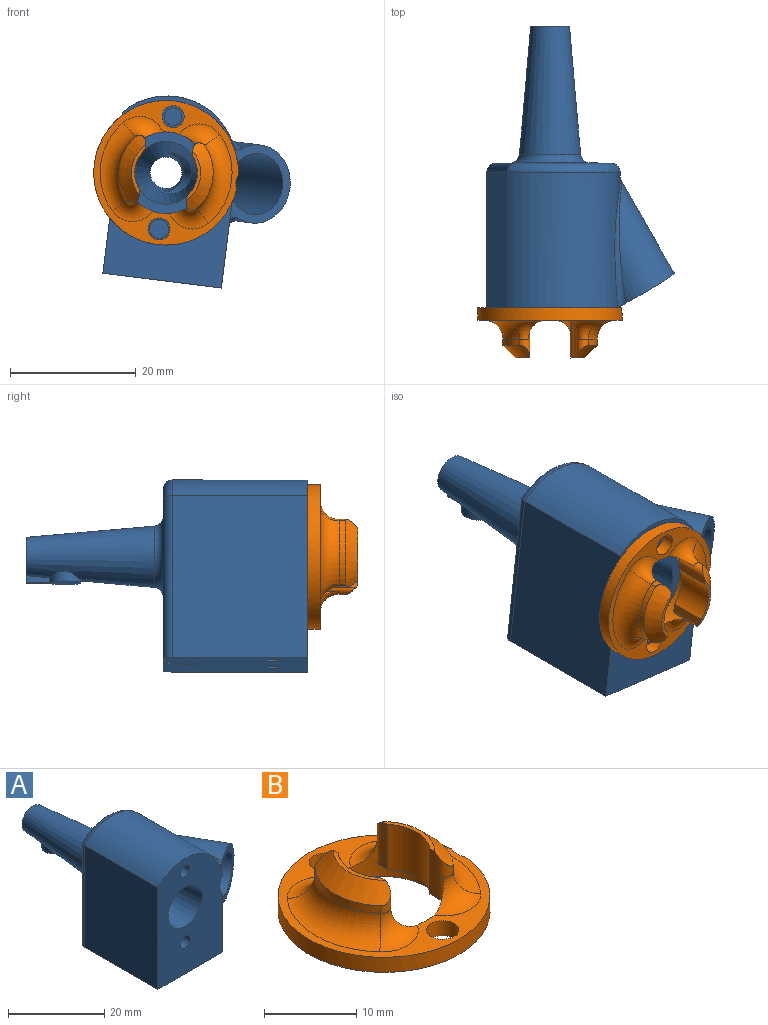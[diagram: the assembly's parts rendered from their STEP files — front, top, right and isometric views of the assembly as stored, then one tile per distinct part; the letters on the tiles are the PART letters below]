
ASSEMBLY  parts=2 mates=1
PART A: 57 faces, bbox 28.6x45.5x30.4 mm
  f0: cone r=5mm half-angle=5deg, axis (0,-1,0), area 490.2mm2, adj f1,f12,f23,f55,f56
  f1: cone r=5mm half-angle=5deg, axis (0,-1,0), area 0.1mm2, adj f0,f24,f56
  f2: cylinder r=11mm len=21.5mm, axis (0,-1,0), area 463.2mm2, adj f5,f6,f49,f51,f54
  f3: plane 23x19mm, normal (0,0,-1), area 420.2mm2, adj f4,f5,f6,f14,f16,f26,f27,f28
  f4: plane 27.83x16mm, normal (0,1,0), area 293mm2, adj f3,f52,f53,f54,f55
  f5: plane 29.34x19.01mm, normal (0,-1,0), area 427.9mm2, adj f2,f3,f6,f7,f9,f10,f13,f19
  f6: plane 21.51x18.34mm, normal (1,0,0), area 241mm2, adj f2,f3,f5,f9,f10,f48,f52
  f7: cylinder r=11mm len=2.65mm, axis (0,-1,0), area 0.5mm2, adj f5,f9,f10
  f8: cylinder r=6.25mm len=19.78mm, axis (0.5,-0.87,0), area 222.2mm2, adj f9,f48,f49
  f9: plane 12.94x9.7mm, normal (0.5,-0.87,0), area 37.3mm2, adj f5,f6,f7,f8,f10,f48,f49
  f10: cylinder r=4.9mm len=25.35mm, axis (0.5,-0.87,0), area 539.8mm2, adj f5,f6,f7,f9,f11,f13,f47,f50
  f11: plane 8.39x2.05mm, normal (0.5,-0.87,0), area 5.8mm2, adj f10,f47
  f12: plane 7.29x6.19mm, normal (0,1,0), area 11.1mm2, adj f0,f18,f23,f24,f25
  f13: cone r=5mm half-angle=5deg, axis (0,-1,0), area 573.5mm2, adj f5,f10,f18,f50
  f14: cylinder r=1.3mm len=10mm, axis (0,0,-1), area 81.7mm2, adj f3,f15
  f15: plane 2.6x2.6mm, normal (0,0,-1), area 5.3mm2, adj f14
  f16: cylinder r=1.3mm len=10mm, axis (0,0,-1), area 81.7mm2, adj f3,f17
  f17: plane 2.6x2.6mm, normal (0,0,-1), area 5.3mm2, adj f16
  f18: cylinder r=2.5mm len=16.23mm, axis (0,-1,0), area 254.9mm2, adj f12,f13
  f19: cylinder r=1.52mm len=10mm, axis (0,-1,0), area 95.4mm2, adj f5,f20
  f20: plane 3.04x3.04mm, normal (0,-1,0), area 7.2mm2, adj f19
  f21: cylinder r=1.4mm len=10mm, axis (0,-1,0), area 88mm2, adj f5,f22
  f22: plane 2.8x2.8mm, normal (0,-1,0), area 6.2mm2, adj f21
  f23: plane 3.77x1.12mm, normal (1,0,0), area 3.6mm2, adj f0,f12,f25,f56
  f24: plane 3.77x1.12mm, normal (-1,0,0), area 3.6mm2, adj f1,f12,f25,f56
  f25: plane 8.75x5mm, normal (0,0,-1), area 21.9mm2, adj f12,f23,f24,f56
  f26: plane 3.2x2mm, normal (0,-1,0), area 6.4mm2, adj f3,f27,f45,f46
  f27: plane 2x0.51mm, normal (-1,0,0), area 1mm2, adj f3,f26,f28,f46
  f28: plane 2.51x2mm, normal (0,1,0), area 5mm2, adj f3,f27,f29,f46
  f29: plane 2x0.03mm, normal (-1,0,0), area 0.1mm2, adj f3,f28,f30,f46
  f30: plane 2x1.07mm, normal (-0.7,-0.71,0), area 3mm2, adj f3,f29,f31,f46
  f31: extruded ~2x1.15mm, area 3mm2, adj f3,f30,f32,f46
  f32: extruded ~2x0.92mm, area 1.9mm2, adj f3,f31,f33,f46
  f33: extruded ~2x0.94mm, area 2.1mm2, adj f3,f32,f34,f46
  f34: extruded ~2x1.08mm, area 2.3mm2, adj f3,f33,f35,f46
  f35: extruded ~2x1.47mm, area 3.2mm2, adj f3,f34,f36,f46
  f36: plane 2x0.38mm, normal (0.79,-0.61,0), area 1mm2, adj f3,f35,f37,f46
  f37: extruded ~2x0.6mm, area 1.4mm2, adj f3,f36,f38,f46
  f38: extruded ~2x0.57mm, area 1.2mm2, adj f3,f37,f39,f46
  f39: extruded ~2x0.66mm, area 1.4mm2, adj f3,f38,f40,f46
  f40: extruded ~2x0.62mm, area 1.4mm2, adj f3,f39,f41,f46
  f41: extruded ~2x0.52mm, area 1.1mm2, adj f3,f40,f42,f46
  f42: extruded ~2x0.49mm, area 1.1mm2, adj f3,f41,f43,f46
  f43: extruded ~2x0.85mm, area 2.3mm2, adj f3,f42,f44,f46
  f44: plane 2x1.29mm, normal (0.71,0.71,0), area 3.6mm2, adj f3,f43,f45,f46
  f45: plane 2x0.48mm, normal (1,0,0), area 1mm2, adj f3,f26,f44,f46
  f46: plane 4.94x3.2mm, normal (0,0,-1), area 5.2mm2, adj f26,f27,f28,f29,f30,f31,f32,f33
  f47: bspline ~13.5x6.29mm, area 43.3mm2, adj f10,f11,f50
  f48: bspline ~20.75x8.48mm, area 28.5mm2, adj f6,f8,f9,f49
  f49: bspline ~21.87x6.97mm, area 22.3mm2, adj f2,f5,f8,f9,f48
  f50: bspline ~10.24x9mm, area 74.8mm2, adj f10,f13,f47
  f51: plane 25.88x21.5mm, normal (-1,0,0), area 556.3mm2, adj f2,f3,f5,f53
  f52: cylinder r=1.5mm len=18.33mm, axis (0,0,-1), area 43.2mm2, adj f3,f4,f6,f54
  f53: cylinder r=1.5mm len=25.88mm, axis (0,0,1), area 60.2mm2, adj f3,f4,f51,f54
  f54: torus R=9.5mm, axis (0,-1,0), area 58mm2, adj f2,f4,f52,f53
  f55: torus R=6.37mm, axis (0,-1,0), area 76.2mm2, adj f0,f4
  f56: cylinder r=2.5mm len=5mm, axis (0,0,-1), area 15.8mm2, adj f0,f1,f23,f24,f25
PART B: 31 faces, bbox 27.4x23x8 mm
  f0: plane 23x22.44mm, normal (0,0,-1), area 252.2mm2, adj f2,f3,f4,f5,f30
  f1: plane 23x22.95mm, normal (0,0,1), area 105.3mm2, adj f2,f3,f4,f5,f22,f23,f24,f25
  f2: cylinder r=6.5mm len=13mm, axis (0,0,1), area 89.5mm2, adj f0,f1,f7,f9,f13,f15,f19,f21
  f3: cylinder r=1.75mm len=3.5mm, axis (0,0,1), area 22mm2, adj f0,f1
  f4: cylinder r=1.75mm len=3.5mm, axis (0,0,1), area 22mm2, adj f0,f1
  f5: cylinder r=11.5mm len=23mm, axis (0,0,1), area 134.7mm2, adj f0,f1,f30
  f6: plane 6.01x1.14mm, normal (1,0,0), area 6.7mm2, adj f7,f11,f12,f13,f28
  f7: cylinder r=1mm len=5.7mm, axis (0,0,-1), area 6.3mm2, adj f2,f6,f8,f13,f27,f28
  f8: cylinder r=7.5mm len=10.13mm, axis (0,0,-1), area 11.1mm2, adj f7,f9,f26,f28
  f9: cylinder r=1mm len=5.7mm, axis (0,0,-1), area 6.3mm2, adj f2,f8,f10,f13,f25,f28
  f10: plane 6.01x1.14mm, normal (1,0,0), area 6.7mm2, adj f9,f11,f12,f13,f28
  f11: cylinder r=5mm len=6.52mm, axis (0,0,-1), area 42.6mm2, adj f6,f10,f12,f13
  f12: plane 7.97x1.71mm, normal (0,0,1), area 4mm2, adj f6,f10,f11,f28
  f13: plane 10.15x2.71mm, normal (0,0,-1), area 14.5mm2, adj f2,f6,f7,f9,f10,f11
  f14: cylinder r=7.5mm len=10.13mm, axis (0,0,-1), area 11.1mm2, adj f15,f19,f23,f29
  f15: cylinder r=1mm len=5.7mm, axis (0,0,-1), area 6.3mm2, adj f2,f14,f16,f21,f22,f29
  f16: plane 6.01x1.14mm, normal (-1,0,0), area 6.7mm2, adj f15,f17,f20,f21,f29
  f17: cylinder r=5mm len=6.52mm, axis (0,0,-1), area 42.6mm2, adj f16,f18,f20,f21
  f18: plane 6.01x1.14mm, normal (-1,0,0), area 6.7mm2, adj f17,f19,f20,f21,f29
  f19: cylinder r=1mm len=5.7mm, axis (0,0,-1), area 6.3mm2, adj f2,f14,f18,f21,f24,f29
  f20: plane 7.97x1.71mm, normal (0,0,1), area 4mm2, adj f16,f17,f18,f29
  f21: plane 10.15x2.71mm, normal (0,0,-1), area 14.5mm2, adj f2,f15,f16,f17,f18,f19
  f22: torus R=4mm, axis (0,0,1), area 17.4mm2, adj f1,f2,f15,f23
  f23: torus R=10.5mm, axis (0,0,1), area 60mm2, adj f1,f14,f22,f24
  f24: torus R=4mm, axis (0,0,1), area 17.4mm2, adj f1,f2,f19,f23
  f25: torus R=4mm, axis (0,0,1), area 17.4mm2, adj f1,f2,f9,f26
  f26: torus R=10.5mm, axis (0,0,1), area 60mm2, adj f1,f8,f25,f27
  f27: torus R=4mm, axis (0,0,1), area 17.4mm2, adj f1,f2,f7,f26
  f28: cone r=5.5mm half-angle=45deg, axis (0,0,-1), area 31.8mm2, adj f6,f7,f8,f9,f10,f12
  f29: cone r=5.5mm half-angle=45deg, axis (0,0,-1), area 31.8mm2, adj f14,f15,f16,f18,f19,f20
  f30: cone r=4.45mm half-angle=45deg, axis (0,0,-1), area 15.3mm2, adj f0,f1,f5
PLACE A rot(axis=(0,1,0),7.1deg) t=(-3.44,-8.78,-0.45)mm
PLACE B rot(axis=(1,0.06,-0.06),90.2deg) t=(-12.23,-10.78,17.88)mm
MATE cylindrical A.f19 <-> B.f3  axis (0,-1,0) through (-13.35,-8.78,8.95)mm
